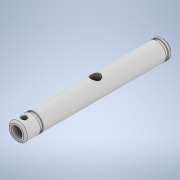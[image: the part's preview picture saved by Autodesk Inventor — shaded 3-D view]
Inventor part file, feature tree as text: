
AUTODESK INVENTOR PART (.ipt)
format: ipt  version: 2022 (Build 260153000, 153)  size: 168,960 bytes
history: native  units: mm
features: sketch x4, extrude x3, thread x2, projected_geometry x2, revolve x1, plane x1
ambient origin geometry x8: Origin, YZ Plane, XZ Plane, XY Plane, X Axis, Y Axis, Z Axis, Center Point
bodies: Solid1 (feature_tree)
feature tree (13):
  revolve  "Revolution1"  [1 undecoded]
  extrude  "Extrusion1"  Depth=1.5mm
  plane  "Work Plane1"
  extrude  "Extrusion2"  Depth=1.5mm
  extrude  "Extrusion3"  TaperAngle=135.0deg  [1 undecoded]
  thread  "Thread1"  [1 undecoded]
  thread  "Thread2"  [1 undecoded]
  sketch  "Sketch1"  dims[d9=80.0mm d10=5.0mm]
  sketch  "Sketch2"  dims[d11=0.5mm d12=1.5mm]
  sketch  "Sketch3"  dims[d13=1.5mm d14=2.0mm]
  projected_geometry  "Projected Loop1"
  sketch  "Sketch4"  dims[d15=1.0mm d16=135.0deg d17=67.0mm d18=135.0deg d19=1.414mm d20=90.0deg d21=6.0mm d22=10.0mm d23=0.0mm d24=5.0mm d25=5.0mm d26=67.0mm d27=33.5mm d28=10.0mm d29=0.0mm d30=3.0mm d31=4.0mm d32=10.0mm d33=0.0mm d34=10.0mm d35=0.0mm d36=10.0mm d37=0.0mm]
  projected_geometry  "Projected Loop2"
note: 4 required parameter values undecoded (feature->parameter linkage not recoverable at this tier; creation-order binding heuristic only, values carry confidence <= 0.55)